# Revit family: Door_Overhead-Sectional-Panel_Haas_No-Inset-Panels
name_source: partatom
category: Doors
units: mm (PartAtom-declared; Revit-internal decimal feet)

## family parameters
Always vertical = Yes
Classification Number = 23.30.10.17.37.14
Cut with Voids When Loaded = No
Room Calculation Point = No
Shared = No
Work Plane-Based = Yes

## types (4) — shared parameters
Assembly Code = B2030410
Default Elevation = 4' - 0"
Description = Haas Door Panel as Specified
Height = 8' - 0"
Keynote = 08360
Manufacturer = Haas Door Co.
Model = Haas Door Panel as Specified
Number Panels = 6
Section Type_Row 1 = HAAS_Section_Flush : Standard
Section Type_Row 10 = HAAS_Section_Flush : Standard
Section Type_Row 2 = HAAS_Section_Flush : Standard
Section Type_Row 3 = HAAS_Section_Flush : Standard
Section Type_Row 5 = HAAS_Section_Flush : Standard
Section Type_Row 6 = HAAS_Section_Flush : Standard
Section Type_Row 7 = HAAS_Section_Flush : Standard
Section Type_Row 8 = HAAS_Section_Flush : Standard
Section Type_Row 9 = HAAS_Section_Flush : Standard
Thickness = 0' - 3"
URL = http://www.haasdoor.com
Width = 10' - 0"

## per-type parameters (varying)
| type | Section Type_Row 4 |
| All Flush | HAAS_Section_Flush : Standard |
| Design A | HAAS_Section_Full Vision : Full Vision |
| Design B | HAAS_Section_TL Vision : 24"x6" Lite |
| Design C | HAAS_Section_TL Vision : 25"x12" Lite |

## geometry (parser evidence)
native form markers: Sweep x12
no freeform markers — native parametric forms only
